# Revit family: gorter_WAG-1000-2000
name_source: partatom
category: Generic Models
revit_build: Autodesk Revit 2017 (Build: 20171027_0315(x64)
units: mm (PartAtom-declared; Revit-internal decimal feet)

## family parameters
Always vertical = Yes
Can host rebar = No
Cut with Voids When Loaded = No
Host = Floor
Part Type = Normal
Room Calculation Point = No
Round Connector Dimension = Use Diameter
Shared = Yes

## types (2) — shared parameters
B = 1000 mm  [stored 3.28084 ft]
C = 400 mm  [stored 1.31234 ft]
frame = <By Category>
glasplaat = Glass
kitvoeg = <By Category>

## per-type parameters (varying)
| type | A |
| WAG-1000-2000 | 2000 mm  [stored 6.56168 ft] |
| WAG-1000-1000 | 1000 mm  [stored 3.28084 ft] |

type visibility flags (boolean, named after types; folded from table):
- WAG-1000-2000: Yes: WAG-1000-2000 (ankers)
- WAG-1000-1000: Yes: (none)

note: [stored X ft] marks values corroborated as IEEE doubles in the binary element streams (Revit-internal decimal feet)

## geometry (parser evidence)
native form markers: Sweep x8
no freeform markers — native parametric forms only
